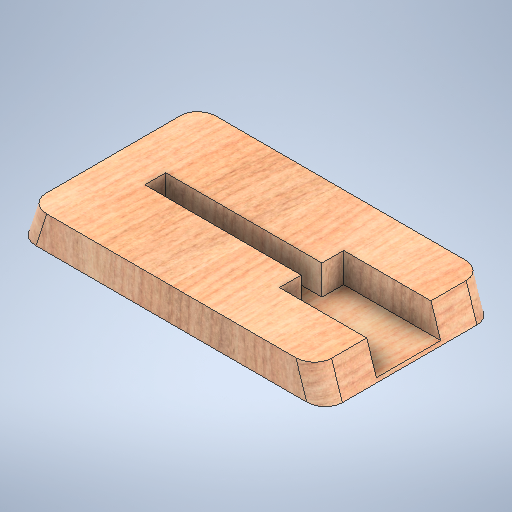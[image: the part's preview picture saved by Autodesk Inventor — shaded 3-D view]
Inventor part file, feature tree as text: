
AUTODESK INVENTOR PART (.ipt)
format: ipt  version: 2025.1 (Build 291241000, 241)  size: 452,608 bytes
history: native  units: mm
features: sketch x4, extrude x3, projected_geometry x2, mirror x1, fillet x1
ambient origin geometry x8: Origin, YZ Plane, XZ Plane, XY Plane, X Axis, Y Axis, Z Axis, Center Point
bodies: Volumenkörper1 (feature_tree)
feature tree (11):
  extrude  "Extrusion1"  Depth=195.0mm
  extrude  "Extrusion2"  Depth=38.0mm TaperAngle=0.0deg
  mirror  "Spiegeln1"
  fillet  "Rundung1"  Radius=15.5mm
  extrude  "Extrusion3"  Depth=20.0mm
  sketch  "Sketch7"  dims[d14=24.0mm d15=74.0mm d16=37.0mm d17=180.0mm d18=34.0mm d19=0.0mm d35=22.0mm d36=21.0mm]
  sketch  "Skizze2"  dims[d0=195.0mm d1=354.0mm]
  sketch  "Skizze3"  dims[d2=38.0mm d3=0.0mm d5=47.0mm d6=0.0mm d7=15.5mm]
  sketch  "Skizze4"  dims[d8=20.0mm d12=113.0mm]
  projected_geometry  "Projizierte Kontur1"
  projected_geometry  "Projected Loop2"
